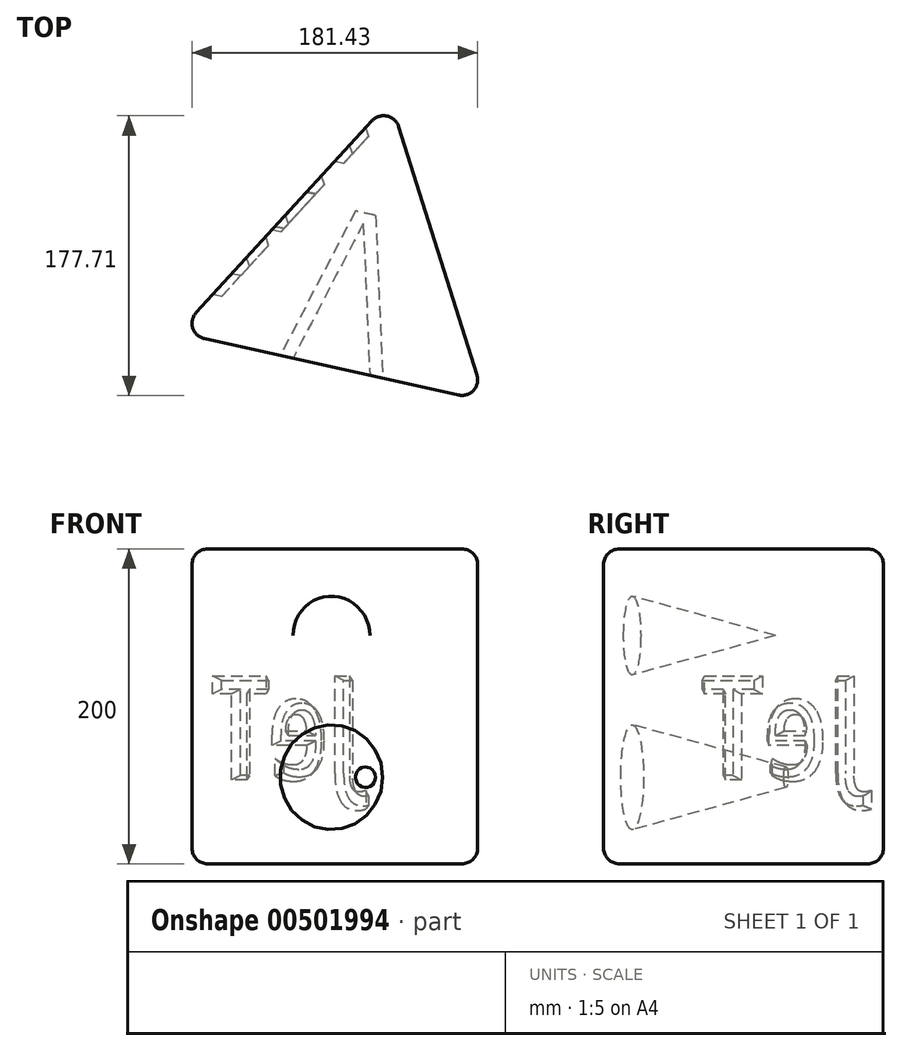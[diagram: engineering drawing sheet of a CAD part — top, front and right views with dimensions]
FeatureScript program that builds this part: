
annotation { "Feature Type Name" : "Feature", "Feature Type Description" : "" }
export const myFeature = defineFeature(function(context is Context, id is Id, definition is map)
    precondition{}
    {
        {
            assignVariable(context, id + "F0", {"name" : "Maat2", "anyValue" : 200});
        }
        {
            var Q0;
            Q0=qCreatedBy(makeId("Top.planeOp"),FACE);
            var sketch = newSketch(context, id + "F1", { "sketchPlane" : qUnion([Q0])});
            skCircle(sketch, "E0.cCircle", {"center": v(0, 0) * mm, "radius": 57.74 * mm, "construction": true});
            skLineSegment(sketch, "E0.0", {"start": v(25.02, 112.73) * mm, "end": v(85.12, -78.03) * mm});
            skLineSegment(sketch, "E0.1", {"start": v(85.12, -78.03) * mm, "end": v(-110.13, -34.7) * mm});
            skLineSegment(sketch, "E0.2", {"start": v(-110.13, -34.7) * mm, "end": v(25.02, 112.73) * mm});
            skPoint(sketch, "E0.0.midPoint", {"position": v(55.07, 17.35) * mm});
            skSolve(sketch);
        }
        {
            var Q0;
            Q0=makeQuery(id+"F1.imprint","IMPRINT",FACE,{"disambiguationData":[TD([[makeQuery(id+"F1.imprint","IMPRINT",EDGE,{"derivedFrom":sQuery(id+"F1.wireOp",EDGE,"E0.0")}),-1.0]])]});
            extrude(context, id + "F2", {"entities" : qUnion([Q0]), "depth" : (getVariable(context, 'Maat2')) * mm});
        }
        {
            var Q0;
            Q0=makeQuery(id+"F2.opExtrude","SWEPT_EDGE",EDGE,{"disambiguationData":[OSD([sQuery(id+"F1.wireOp",EDGE,"E0.0"),sQuery(id+"F1.wireOp",EDGE,"E0.2")])]});
            var Q1;
            Q1=makeQuery(id+"F2.opExtrude","SWEPT_EDGE",EDGE,{"disambiguationData":[OSD([sQuery(id+"F1.wireOp",EDGE,"E0.1"),sQuery(id+"F1.wireOp",EDGE,"E0.2")])]});
            var Q2;
            Q2=makeQuery(id+"F2.opExtrude","SWEPT_EDGE",EDGE,{"disambiguationData":[OSD([sQuery(id+"F1.wireOp",EDGE,"E0.0"),sQuery(id+"F1.wireOp",EDGE,"E0.1")])]});
            var Q3;
            Q3=makeQuery(id+"F2.opExtrude","CAP_FACE",FACE,{"disambiguationData":[OSD([sQuery(id+"F1.wireOp",EDGE,"E0.0"),sQuery(id+"F1.wireOp",EDGE,"E0.1"),sQuery(id+"F1.wireOp",EDGE,"E0.2")])],"isStart":false});
            var Q4;
            Q4=makeQuery(id+"F2.opExtrude","CAP_FACE",FACE,{"disambiguationData":[OSD([sQuery(id+"F1.wireOp",EDGE,"E0.0"),sQuery(id+"F1.wireOp",EDGE,"E0.1"),sQuery(id+"F1.wireOp",EDGE,"E0.2")])],"isStart":true});
            fillet(context, id + "F3", {"entities" : qUnion([Q0, Q1, Q2, Q3, Q4]), "radius" : 10 * mm, "tangentPropagation" : true, "allowEdgeOverflow" : false});
        }
        {
            var Q0;
            Q0=makeQuery(id+"F2.opExtrude","SWEPT_FACE",FACE,{"disambiguationData":[OSD([sQuery(id+"F1.wireOp",EDGE,"E0.1")])]});
            var sketch = newSketch(context, id + "F4", { "sketchPlane" : qUnion([Q0])});
            skLineSegment(sketch, "E1.0.0", {"start": v(-82.68, 190) * mm, "end": v(-82.68, 10) * mm, "construction": true});
            skLineSegment(sketch, "E1.0.1", {"start": v(-82.68, 10) * mm, "end": v(82.68, 10) * mm, "construction": true});
            skLineSegment(sketch, "E1.0.2", {"start": v(82.68, 10) * mm, "end": v(82.68, 190) * mm, "construction": true});
            skLineSegment(sketch, "E1.0.3", {"start": v(82.68, 190) * mm, "end": v(-82.68, 190) * mm, "construction": true});
            skLineSegment(sketch, "E2", {"start": v(82.68, 100) * mm, "end": v(-82.68, 190) * mm, "construction": true});
            skLineSegment(sketch, "E3", {"start": v(-82.68, 10) * mm, "end": v(82.68, 100) * mm, "construction": true});
            skPoint(sketch, "E4", {"position": v(0, 145) * mm});
            skPoint(sketch, "E5", {"position": v(0, 55) * mm});
            skCircle(sketch, "E6", {"center": v(0, 145) * mm, "radius": 25 * mm});
            skCircle(sketch, "E7", {"center": v(0, 55) * mm, "radius": 33.33 * mm});
            skSolve(sketch);
        }
        {
            var Q0;
            Q0=makeQuery(id+"F4.imprint","IMPRINT",FACE,{"disambiguationData":[TD([[makeQuery(id+"F4.imprint","IMPRINT",EDGE,{"derivedFrom":sQuery(id+"F4.wireOp",EDGE,"E6")}),1.0]])]});
            var Q1;
            Q1=makeQuery(id+"F4.imprint","IMPRINT",FACE,{"disambiguationData":[TD([[makeQuery(id+"F4.imprint","IMPRINT",EDGE,{"derivedFrom":sQuery(id+"F4.wireOp",EDGE,"E7")}),1.0]])]});
            extrude(context, id + "F5", {"entities" : qUnion([Q0, Q1]), "operationType" : NewBodyOperationType.REMOVE, "oppositeDirection" : true, "depth" : 100 * mm, "hasDraft" : true, "draftAngle" : 15 * degree, "draftPullDirection" : true});
        }
        {
            var Q0;
            Q0=makeQuery(id+"F2.opExtrude","SWEPT_FACE",FACE,{"disambiguationData":[OSD([sQuery(id+"F1.wireOp",EDGE,"E0.2")])]});
            var sketch = newSketch(context, id + "F6", { "sketchPlane" : qUnion([Q0])});
            skText(sketch, "E8", { "text": "JeT", "fontName": "OpenSans-Bold.ttf"});
            const initialGuessF6  = {"E8": [-0.07, 0.05333, 1, 0, 0.06667]};
            skSetInitialGuess(sketch, initialGuessF6);
            skSolve(sketch);
        }
        {
            var Q0;
            Q0 = qSketchRegion(id + "F6", true);
            extrude(context, id + "F7", {"entities" : qUnion([Q0]), "operationType" : NewBodyOperationType.REMOVE, "oppositeDirection" : true, "depth" : 5 * mm, "hasDraft" : true, "draftAngle" : 30 * degree, "draftPullDirection" : true});
        }
    });
